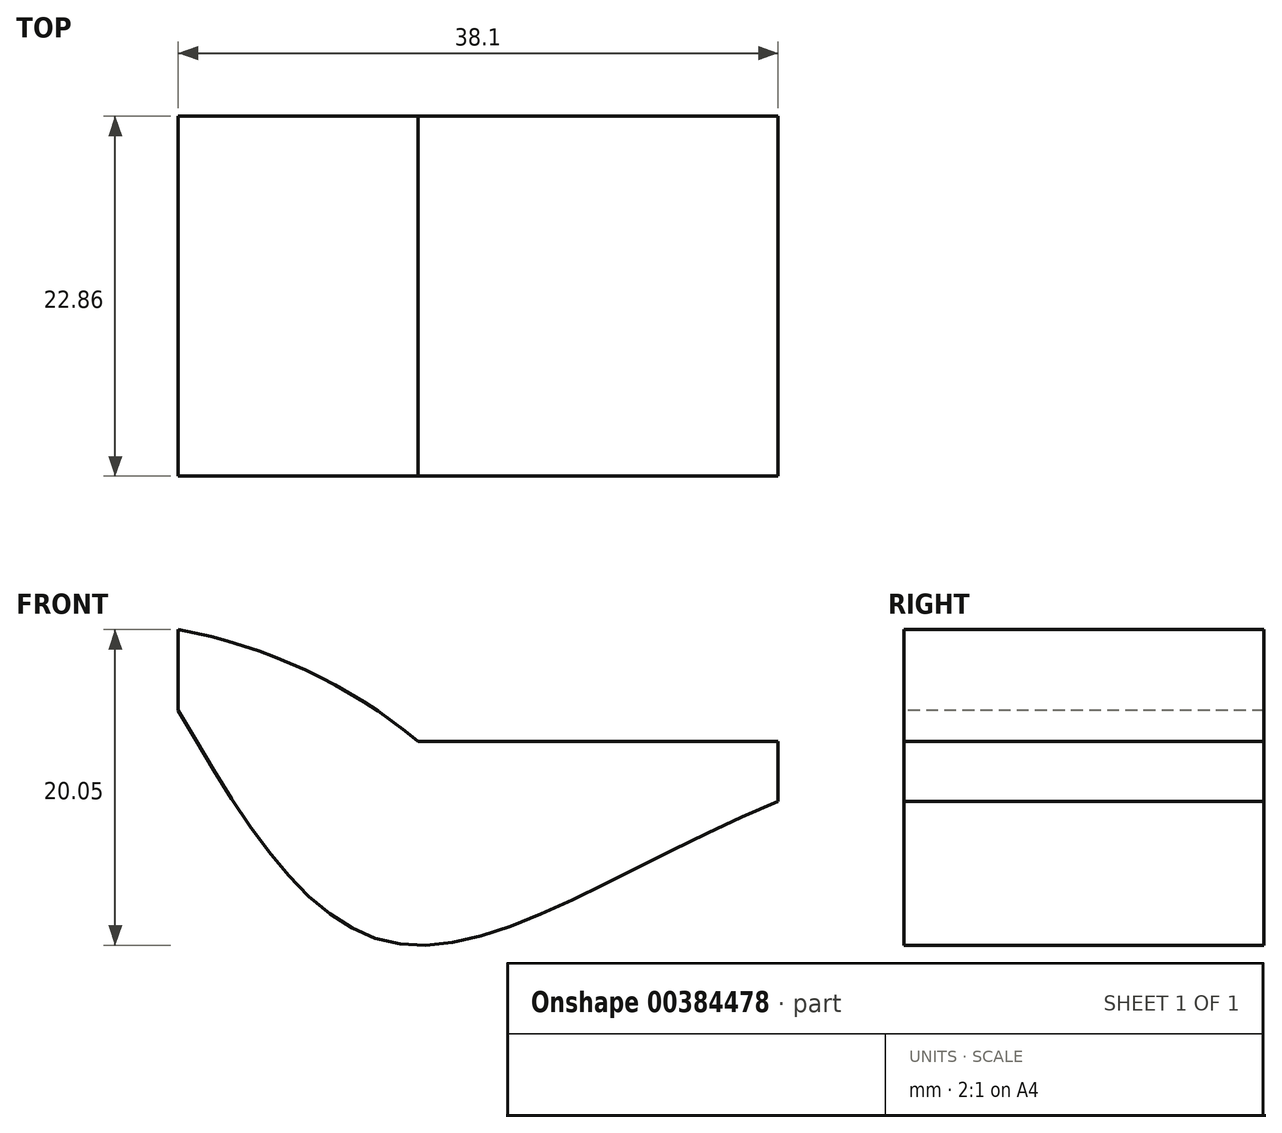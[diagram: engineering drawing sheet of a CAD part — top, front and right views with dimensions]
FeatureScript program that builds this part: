
annotation { "Feature Type Name" : "Feature", "Feature Type Description" : "" }
export const myFeature = defineFeature(function(context is Context, id is Id, definition is map)
    precondition{}
    {
        {
            var Q0;
            Q0=qCreatedBy(makeId("Top.planeOp"),FACE);
            var sketch = newSketch(context, id + "F0", { "sketchPlane" : qUnion([Q0])});
            skLineSegment(sketch, "E0.bottom", {"start": v(0, 0) * mm, "end": v(38.1, 0) * mm});
            skLineSegment(sketch, "E0.top", {"start": v(0, -22.86) * mm, "end": v(38.1, -22.86) * mm});
            skLineSegment(sketch, "E0.left", {"start": v(0, 0) * mm, "end": v(0, -22.86) * mm});
            skLineSegment(sketch, "E0.right", {"start": v(38.1, 0) * mm, "end": v(38.1, -22.86) * mm});
            skSolve(sketch);
        }
        {
            var Q0;
            Q0 = qSketchRegion(id + "F0", true);
            extrude(context, id + "F1", {"entities" : qUnion([Q0]), "depth" : 33.02 * mm});
        }
        {
            var Q0;
            Q0=makeQuery(id+"F1.opExtrude","SWEPT_FACE",FACE,{"disambiguationData":[OSD([sQuery(id+"F0.wireOp",EDGE,"E0.top")])]});
            cPlane(context, id + "F2", {"entities" : qUnion([Q0]), "cplaneType" : CPlaneType.OFFSET, "offset" : 0 * mm, "width" : 152.4 * mm, "height" : 152.4 * mm});
        }
        {
            var Q0;
            Q0=makeQuery(id+"F1.opExtrude","SWEPT_FACE",FACE,{"disambiguationData":[OSD([sQuery(id+"F0.wireOp",EDGE,"E0.top")])]});
            var sketch = newSketch(context, id + "F3", { "sketchPlane" : qUnion([Q0])});
            skLineSegment(sketch, "E1", {"start": v(0, 0) * mm, "end": v(0, 27.94) * mm});
            skLineSegment(sketch, "E2", {"start": v(38.1, 33.02) * mm, "end": v(38.1, 20.32) * mm});
            skLineSegment(sketch, "E3", {"start": v(38.1, 20.32) * mm, "end": v(15.24, 20.32) * mm});
            skLineSegment(sketch, "E4", {"start": v(0, 27.94) * mm, "end": v(15.24, 27.94) * mm});
            skLineSegment(sketch, "E5", {"start": v(15.24, 27.94) * mm, "end": v(15.24, 20.32) * mm});
            skFitSpline(sketch, "E6", {"points": [v(0, 22.3) * mm, v(13.71, 7.5) * mm, v(38.1, 16.51) * mm, v(73.03, 22.7) * mm], "startDerivative": vector(41.72, -71.48) * mm, "endDerivative": vector(93.94, 6.93) * mm});
            skSolve(sketch);
        }
        {
            var Q0;
            Q0 = qSketchRegion(id + "F3", true);
            var Q1;
            {var subQ1=sQuery(id+"F0.wireOp",EDGE,"E0.top");var subQ2=makeQuery(id+"F1.opExtrude","CAP_EDGE",EDGE,{"disambiguationData":[OSD([subQ1])],"isStart":true});Q1=makeQuery(id+"F3.imprint","IMPRINT",FACE,{"disambiguationData":[TD([[makeQuery(id+"F3.imprint","IMPRINT",EDGE,{"derivedFrom":subQ2}),1.0]])]});}
            var Q2;
            Q2=makeQuery(id+"F3.imprint","IMPRINT",FACE,{"disambiguationData":[TD([[makeQuery(id+"F3.imprint","IMPRINT",EDGE,{"derivedFrom":sQuery(id+"F3.wireOp",EDGE,"E2")}),-1.0]])]});
            extrude(context, id + "F4", {"entities" : qUnion([Q0, Q1, Q2]), "operationType" : NewBodyOperationType.REMOVE, "oppositeDirection" : true, "depth" : 25.4 * mm});
        }
        {
            var Q0;
            Q0=makeQuery(id+"F4.boolean.opBoolean","COPY",EDGE,{"derivedFrom":makeQuery(id+"F4.opExtrude","SWEPT_EDGE",EDGE,{"disambiguationData":[OSD([sQuery(id+"F3.wireOp",EDGE,"E4"),sQuery(id+"F3.wireOp",EDGE,"E5")])]})});
            fillet(context, id + "F5", {"entities" : qUnion([Q0]), "radius" : 33.02 * mm, "tangentPropagation" : true, "allowEdgeOverflow" : false});
        }
    });
